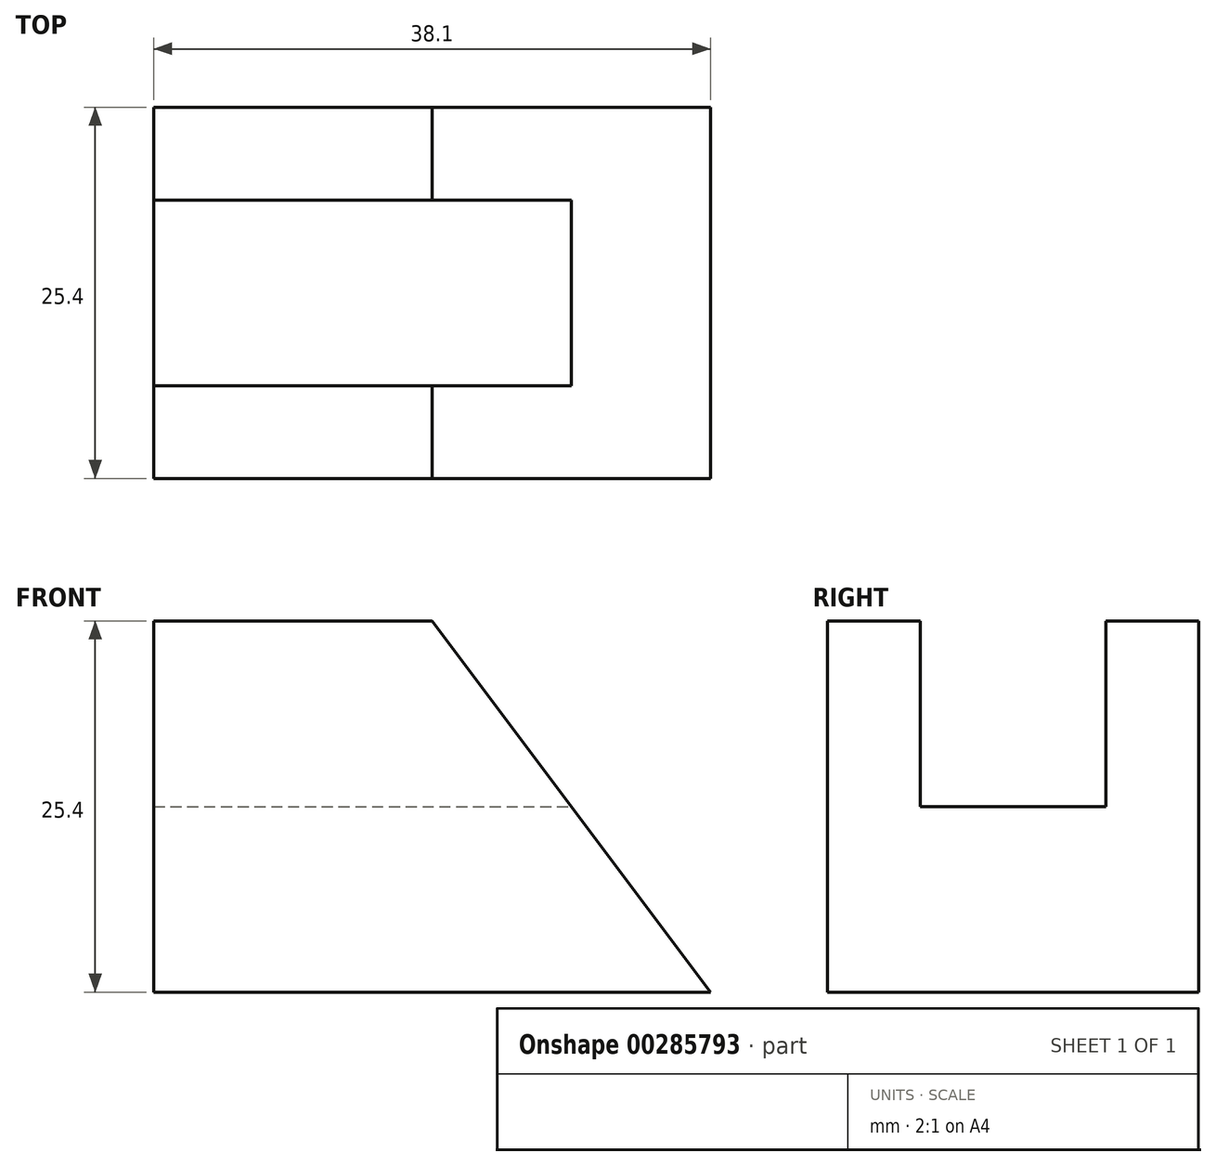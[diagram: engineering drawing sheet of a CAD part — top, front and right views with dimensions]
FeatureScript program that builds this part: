
annotation { "Feature Type Name" : "Feature", "Feature Type Description" : "" }
export const myFeature = defineFeature(function(context is Context, id is Id, definition is map)
    precondition{}
    {
        {
            var Q0;
            Q0=qCreatedBy(makeId("Front.planeOp"),FACE);
            var sketch = newSketch(context, id + "F0", { "sketchPlane" : qUnion([Q0])});
            skLineSegment(sketch, "E0", {"start": v(0, 0) * mm, "end": v(0, 25.4) * mm});
            skLineSegment(sketch, "E1", {"start": v(0, 25.4) * mm, "end": v(19.05, 25.4) * mm});
            skLineSegment(sketch, "E2", {"start": v(19.05, 25.4) * mm, "end": v(38.1, 0) * mm});
            skLineSegment(sketch, "E3", {"start": v(38.1, 0) * mm, "end": v(0, 0) * mm});
            skSolve(sketch);
        }
        {
            var Q0;
            Q0 = qSketchRegion(id + "F0", true);
            extrude(context, id + "F1", {"entities" : qUnion([Q0]), "oppositeDirection" : true, "depth" : 25.4 * mm});
        }
        {
            var Q0;
            Q0=makeQuery(id+"F1.opExtrude","SWEPT_FACE",FACE,{"disambiguationData":[OSD([sQuery(id+"F0.wireOp",EDGE,"E1")])]});
            var sketch = newSketch(context, id + "F2", { "sketchPlane" : qUnion([Q0])});
            skLineSegment(sketch, "E4.bottom", {"start": v(0, 0) * mm, "end": v(19.05, 0) * mm});
            skLineSegment(sketch, "E4.top", {"start": v(0, 6.35) * mm, "end": v(19.05, 6.35) * mm});
            skLineSegment(sketch, "E4.left", {"start": v(0, 0) * mm, "end": v(0, 6.35) * mm});
            skLineSegment(sketch, "E4.right", {"start": v(19.05, 0) * mm, "end": v(19.05, 6.35) * mm});
            skLineSegment(sketch, "E5.bottom", {"start": v(0, 25.4) * mm, "end": v(19.05, 25.4) * mm});
            skLineSegment(sketch, "E5.top", {"start": v(0, 19.05) * mm, "end": v(19.05, 19.05) * mm});
            skLineSegment(sketch, "E5.left", {"start": v(0, 25.4) * mm, "end": v(0, 19.05) * mm});
            skLineSegment(sketch, "E5.right", {"start": v(19.05, 25.4) * mm, "end": v(19.05, 19.05) * mm});
            skLineSegment(sketch, "E6", {"start": v(0, 19.05) * mm, "end": v(0, 6.35) * mm});
            skLineSegment(sketch, "E7", {"start": v(19.05, 19.05) * mm, "end": v(19.05, 6.35) * mm});
            skSolve(sketch);
        }
        {
            var Q0;
            Q0=makeQuery(id+"F2.imprint","IMPRINT",FACE,{"disambiguationData":[TD([[makeQuery(id+"F2.imprint","IMPRINT",EDGE,{"derivedFrom":sQuery(id+"F2.wireOp",EDGE,"E4.top")}),1.0]])]});
            extrude(context, id + "F3", {"entities" : qUnion([Q0]), "operationType" : NewBodyOperationType.REMOVE, "oppositeDirection" : true, "depth" : 12.7 * mm});
        }
        {
            var Q0;
            Q0=makeQuery(id+"F3.boolean.opBoolean","COPY",FACE,{"derivedFrom":makeQuery(id+"F3.opExtrude","SWEPT_FACE",FACE,{"disambiguationData":[OSD([sQuery(id+"F2.wireOp",EDGE,"E7")])]})});
            extrude(context, id + "F4", {"entities" : qUnion([Q0]), "operationType" : NewBodyOperationType.REMOVE, "oppositeDirection" : true, "depth" : 25.4 * mm});
        }
    });
